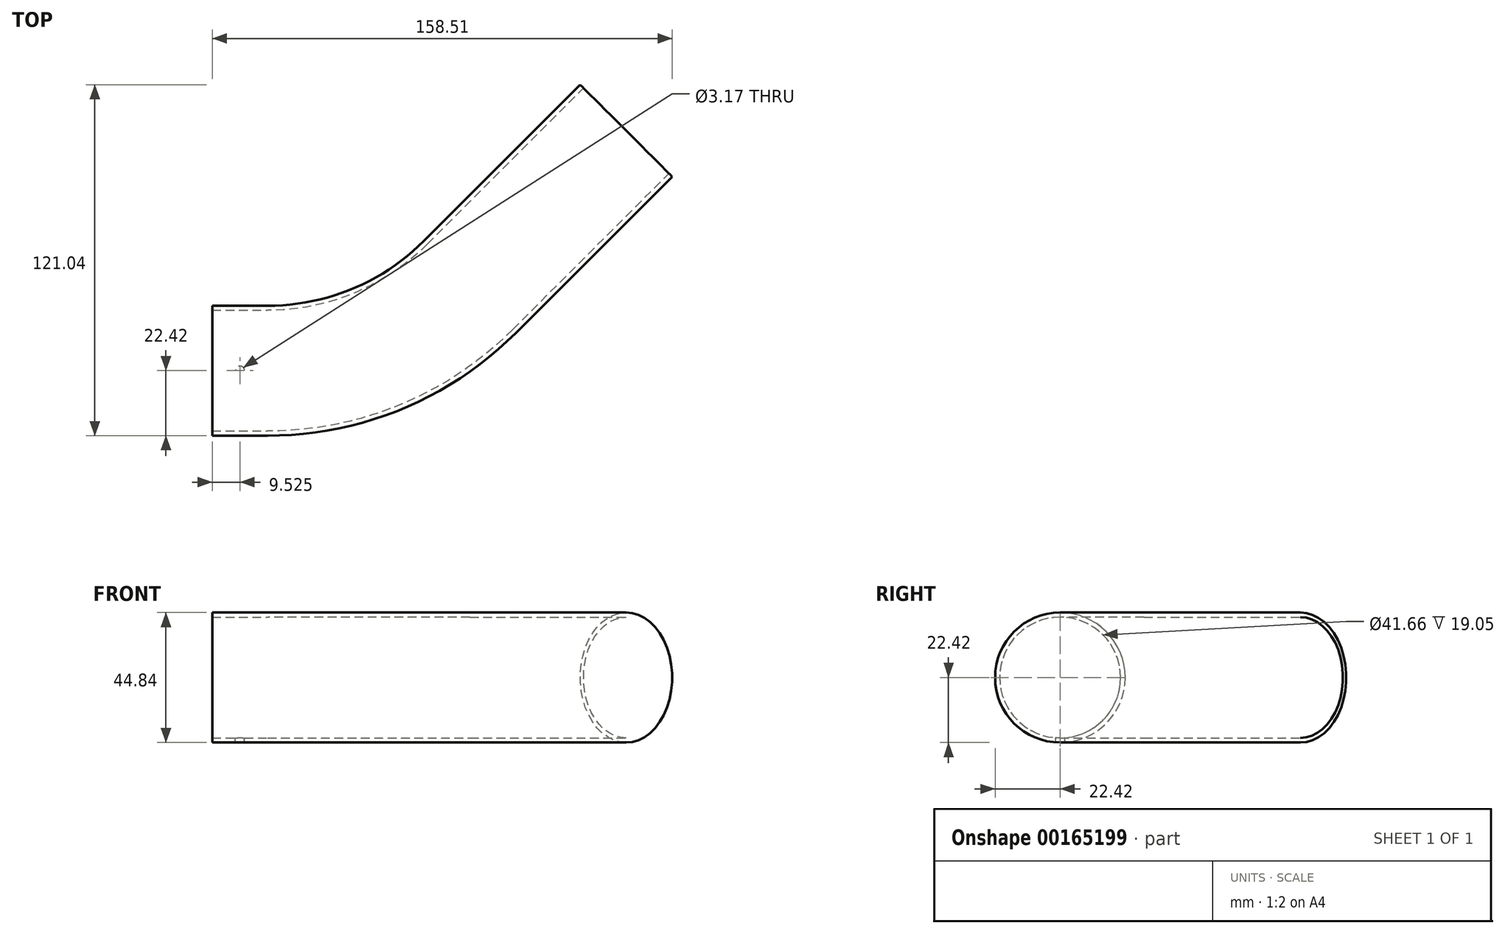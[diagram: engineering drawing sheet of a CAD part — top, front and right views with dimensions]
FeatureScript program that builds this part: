
annotation { "Feature Type Name" : "Feature", "Feature Type Description" : "" }
export const myFeature = defineFeature(function(context is Context, id is Id, definition is map)
    precondition{}
    {
        {
            var Q0;
            Q0=qCreatedBy(makeId("Top.planeOp"),FACE);
            var sketch = newSketch(context, id + "F0", { "sketchPlane" : qUnion([Q0])});
            skLineSegment(sketch, "E0", {"start": v(0, 0) * mm, "end": v(19.05, 0) * mm});
            skArc(sketch, "E1", {"start": v(19.05, 0) * mm, "mid": v(56.79, 7.5) * mm, "end": v(88.78, 28.88) * mm});
            skLineSegment(sketch, "E2", {"start": v(0, 0) * mm, "end": v(0, 22.42) * mm, "construction": true});
            skLineSegment(sketch, "E3", {"start": v(0, 22.42) * mm, "end": v(19.05, 22.42) * mm, "construction": true});
            skLineSegment(sketch, "E4", {"start": v(72.93, 44.73) * mm, "end": v(126.81, 98.62) * mm, "construction": true});
            skLineSegment(sketch, "E5", {"start": v(126.81, 98.62) * mm, "end": v(142.66, 82.77) * mm, "construction": true});
            skArc(sketch, "E6", {"start": v(19.05, 22.42) * mm, "mid": v(48.21, 28.22) * mm, "end": v(72.93, 44.73) * mm, "construction": true});
            skLineSegment(sketch, "E7", {"start": v(88.78, 28.88) * mm, "end": v(142.66, 82.77) * mm});
            skLineSegment(sketch, "E8", {"start": v(19.05, 0) * mm, "end": v(59.9, 0) * mm, "construction": true});
            skLineSegment(sketch, "E9", {"start": v(59.9, 0) * mm, "end": v(88.78, 28.88) * mm, "construction": true});
            skSolve(sketch);
        }
        {
            var Q0;
            Q0=qCreatedBy(makeId("Right.planeOp"),FACE);
            var sketch = newSketch(context, id + "F1", { "sketchPlane" : qUnion([Q0])});
            skCircle(sketch, "E10", {"center": v(0, 0) * mm, "radius": 20.83 * mm});
            skCircle(sketch, "E11", {"center": v(0, 0) * mm, "radius": 22.42 * mm});
            skSolve(sketch);
        }
        {
            var Q0;
            Q0=makeQuery(id+"F1.imprint","IMPRINT",FACE,{"disambiguationData":[TD([[makeQuery(id+"F1.imprint","IMPRINT",EDGE,{"derivedFrom":sQuery(id+"F1.wireOp",EDGE,"E10")}),-1.0]])]});
            var Q1;
            Q1=sQuery(id+"F0.wireOp",EDGE,"E0");
            var Q2;
            Q2=sQuery(id+"F0.wireOp",EDGE,"E1");
            var Q3;
            Q3=sQuery(id+"F0.wireOp",EDGE,"E7");
            sweep(context, id + "F2", {"profiles" : qUnion([Q0]), "path" : qUnion([Q1, Q2, Q3])});
        }
        {
            var Q0;
            Q0=qCreatedBy(makeId("Top.planeOp"),FACE);
            var sketch = newSketch(context, id + "F3", { "sketchPlane" : qUnion([Q0])});
            skLineSegment(sketch, "E12", {"start": v(0, 0) * mm, "end": v(19.05, 0) * mm, "construction": true});
            skCircle(sketch, "E13", {"center": v(9.53, 0) * mm, "radius": 1.59 * mm});
            skSolve(sketch);
        }
        {
            var Q0;
            Q0 = qSketchRegion(id + "F3", true);
            var Q1;
            Q1=makeQuery(id+"F2.opSweep","SWEPT_FACE",FACE,{"disambiguationData":[OSD([sQuery(id+"F0.wireOp",EDGE,"E0"),sQuery(id+"F1.wireOp",EDGE,"E11")])]});
            extrude(context, id + "F4", {"entities" : qUnion([Q0]), "operationType" : NewBodyOperationType.REMOVE, "endBound" : BoundingType.UP_TO_SURFACE, "oppositeDirection" : true, "endBoundEntityFace" : qUnion([Q1]), "depth" : 25.4 * mm});
        }
    });
